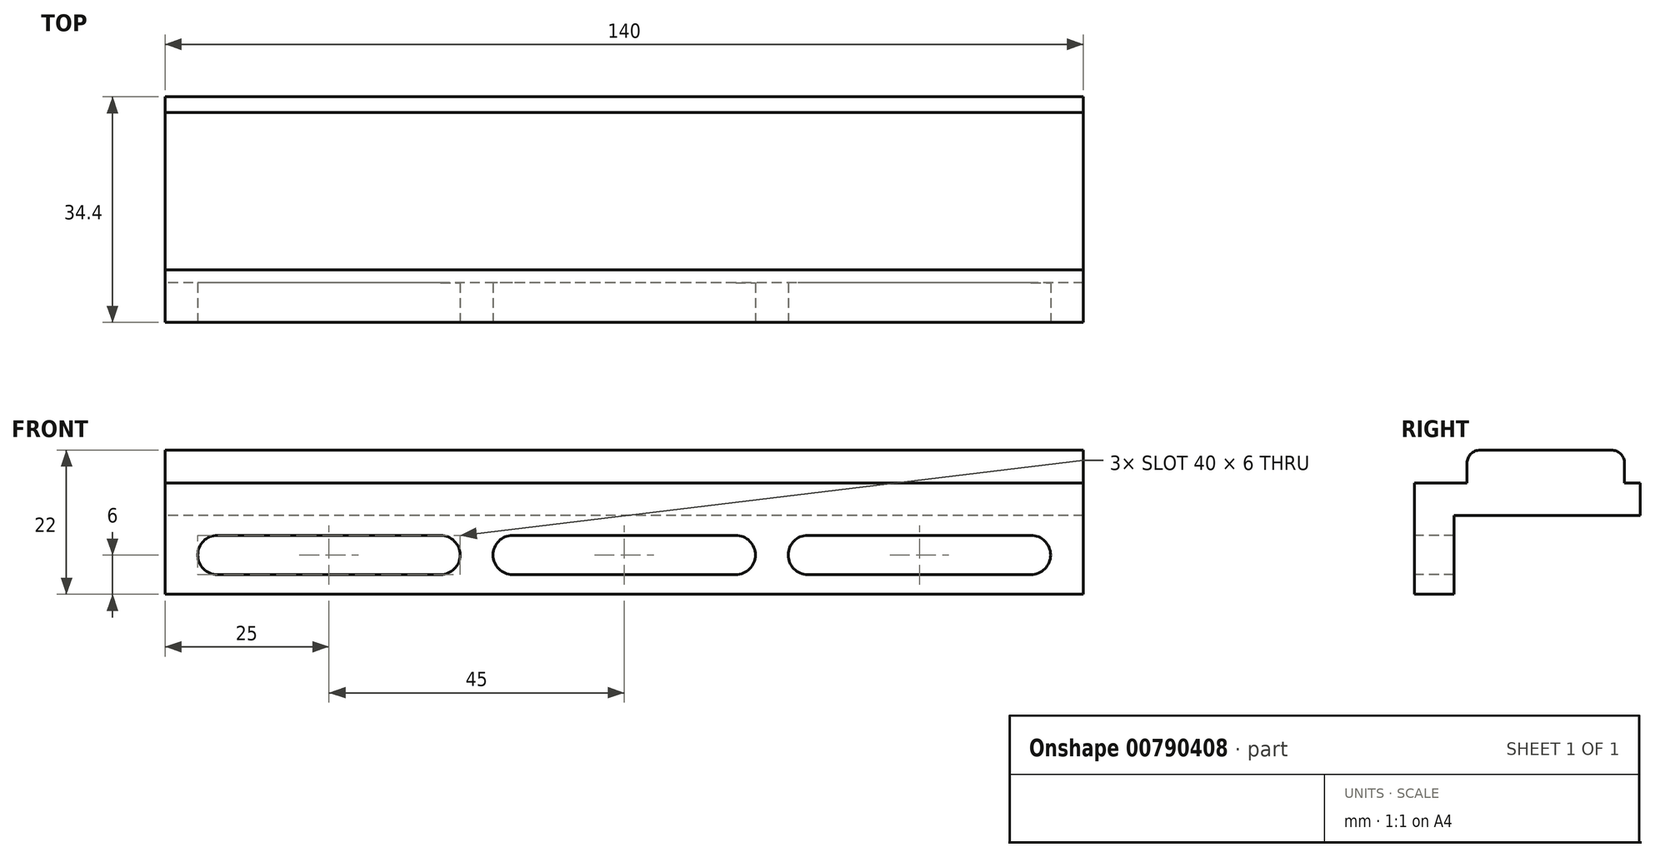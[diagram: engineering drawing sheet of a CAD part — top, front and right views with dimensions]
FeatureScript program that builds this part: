
annotation { "Feature Type Name" : "Feature", "Feature Type Description" : "" }
export const myFeature = defineFeature(function(context is Context, id is Id, definition is map)
    precondition{}
    {
        {
            var Q0;
            Q0=qCreatedBy(makeId("Right.planeOp"),FACE);
            var sketch = newSketch(context, id + "F0", { "sketchPlane" : qUnion([Q0])});
            skLineSegment(sketch, "E0", {"start": v(-20, -12) * mm, "end": v(-20, 5) * mm});
            skLineSegment(sketch, "E1", {"start": v(-20, 5) * mm, "end": v(-12, 5) * mm});
            skLineSegment(sketch, "E2", {"start": v(-12, 5) * mm, "end": v(-12, 10) * mm});
            skLineSegment(sketch, "E3", {"start": v(-12, 10) * mm, "end": v(12, 10) * mm});
            skLineSegment(sketch, "E4", {"start": v(12, 10) * mm, "end": v(12, 5) * mm});
            skLineSegment(sketch, "E5", {"start": v(12, 5) * mm, "end": v(14.4, 5) * mm});
            skLineSegment(sketch, "E6", {"start": v(14.4, 5) * mm, "end": v(14.4, 0) * mm});
            skLineSegment(sketch, "E7", {"start": v(14.4, 0) * mm, "end": v(-14, 0) * mm});
            skLineSegment(sketch, "E8", {"start": v(-14, 0) * mm, "end": v(-14, -12) * mm});
            skLineSegment(sketch, "E9", {"start": v(-14, -12) * mm, "end": v(-20, -12) * mm});
            skLineSegment(sketch, "E10", {"start": v(0, 10) * mm, "end": v(0, 0) * mm, "construction": true});
            skSolve(sketch);
        }
        {
            var Q0;
            Q0=makeQuery(id+"F0.imprint","IMPRINT",FACE,{"disambiguationData":[TD([[makeQuery(id+"F0.imprint","IMPRINT",EDGE,{"derivedFrom":sQuery(id+"F0.wireOp",EDGE,"E0")}),-1.0]])]});
            extrude(context, id + "F1", {"entities" : qUnion([Q0]), "endBound" : BoundingType.SYMMETRIC, "depth" : 140 * mm, "offsetDistance" : 25 * mm});
        }
        {
            var Q0;
            Q0=makeQuery(id+"F1.opExtrude","SWEPT_EDGE",EDGE,{"disambiguationData":[OSD([sQuery(id+"F0.wireOp",EDGE,"E2"),sQuery(id+"F0.wireOp",EDGE,"E3")])]});
            var Q1;
            Q1=makeQuery(id+"F1.opExtrude","SWEPT_EDGE",EDGE,{"disambiguationData":[OSD([sQuery(id+"F0.wireOp",EDGE,"E3"),sQuery(id+"F0.wireOp",EDGE,"E4")])]});
            fillet(context, id + "F2", {"entities" : qUnion([Q0, Q1]), "radius" : 2 * mm, "tangentPropagation" : true, "allowEdgeOverflow" : false});
        }
        {
            var Q0;
            Q0=makeQuery(id+"F1.opExtrude","SWEPT_FACE",FACE,{"disambiguationData":[OSD([sQuery(id+"F0.wireOp",EDGE,"E0")])]});
            var sketch = newSketch(context, id + "F3", { "sketchPlane" : qUnion([Q0])});
            skLineSegment(sketch, "E11", {"start": v(-70, -6) * mm, "end": v(70, -6) * mm, "construction": true});
            skLineSegment(sketch, "E12.bottom", {"start": v(-62, -3) * mm, "end": v(-28, -3) * mm});
            skLineSegment(sketch, "E12.top", {"start": v(-62, -9) * mm, "end": v(-28, -9) * mm});
            skLineSegment(sketch, "E12.left", {"start": v(-65, -6) * mm, "end": v(-65, -6) * mm});
            skLineSegment(sketch, "E12.right", {"start": v(-25, -6) * mm, "end": v(-25, -6) * mm});
            skPoint(sketch, "E13.visualSharp", {"position": v(-65, -3) * mm});
            skArc(sketch, "E13.filletArc", {"start": v(-62, -3) * mm, "mid": v(-64.12, -3.88) * mm, "end": v(-65, -6) * mm});
            skPoint(sketch, "E14.visualSharp", {"position": v(-65, -9) * mm});
            skArc(sketch, "E14.filletArc", {"start": v(-65, -6) * mm, "mid": v(-64.12, -8.12) * mm, "end": v(-62, -9) * mm});
            skPoint(sketch, "E15.visualSharp", {"position": v(-25, -9) * mm});
            skArc(sketch, "E15.filletArc", {"start": v(-28, -9) * mm, "mid": v(-25.88, -8.12) * mm, "end": v(-25, -6) * mm});
            skPoint(sketch, "E16.visualSharp", {"position": v(-25, -3) * mm});
            skArc(sketch, "E16.filletArc", {"start": v(-25, -6) * mm, "mid": v(-25.88, -3.88) * mm, "end": v(-28, -3) * mm});
            skArc(sketch, "E17.1.0.0", {"start": v(-17, -3) * mm, "mid": v(-19.12, -3.88) * mm, "end": v(-20, -6) * mm});
            skArc(sketch, "E17.1.0.1", {"start": v(-20, -6) * mm, "mid": v(-19.12, -8.12) * mm, "end": v(-17, -9) * mm});
            skLineSegment(sketch, "E17.1.0.2", {"start": v(-17, -9) * mm, "end": v(17, -9) * mm});
            skLineSegment(sketch, "E17.1.0.3", {"start": v(-17, -3) * mm, "end": v(17, -3) * mm});
            skArc(sketch, "E17.1.0.4", {"start": v(20, -6) * mm, "mid": v(19.12, -3.88) * mm, "end": v(17, -3) * mm});
            skArc(sketch, "E17.1.0.5", {"start": v(17, -9) * mm, "mid": v(19.12, -8.12) * mm, "end": v(20, -6) * mm});
            skArc(sketch, "E17.2.0.0", {"start": v(28, -3) * mm, "mid": v(25.88, -3.88) * mm, "end": v(25, -6) * mm});
            skArc(sketch, "E17.2.0.1", {"start": v(25, -6) * mm, "mid": v(25.88, -8.12) * mm, "end": v(28, -9) * mm});
            skLineSegment(sketch, "E17.2.0.2", {"start": v(28, -9) * mm, "end": v(62, -9) * mm});
            skLineSegment(sketch, "E17.2.0.3", {"start": v(28, -3) * mm, "end": v(62, -3) * mm});
            skArc(sketch, "E17.2.0.4", {"start": v(65, -6) * mm, "mid": v(64.12, -3.88) * mm, "end": v(62, -3) * mm});
            skArc(sketch, "E17.2.0.5", {"start": v(62, -9) * mm, "mid": v(64.12, -8.12) * mm, "end": v(65, -6) * mm});
            skLineSegment(sketch, "E17.direction1", {"start": v(-65, -6) * mm, "end": v(-20, -6) * mm, "construction": true});
            skSolve(sketch);
        }
        {
            var Q0;
            Q0=makeQuery(id+"F3.imprint","IMPRINT",FACE,{"disambiguationData":[TD([[makeQuery(id+"F3.imprint","IMPRINT",EDGE,{"derivedFrom":sQuery(id+"F3.wireOp",EDGE,"E12.bottom")}),-1.0]])]});
            var Q1;
            Q1=makeQuery(id+"F3.imprint","IMPRINT",FACE,{"disambiguationData":[TD([[makeQuery(id+"F3.imprint","IMPRINT",EDGE,{"derivedFrom":sQuery(id+"F3.wireOp",EDGE,"E17.1.0.0")}),1.0]])]});
            var Q2;
            Q2=makeQuery(id+"F3.imprint","IMPRINT",FACE,{"disambiguationData":[TD([[makeQuery(id+"F3.imprint","IMPRINT",EDGE,{"derivedFrom":sQuery(id+"F3.wireOp",EDGE,"E17.2.0.0")}),1.0]])]});
            extrude(context, id + "F4", {"entities" : qUnion([Q0, Q1, Q2]), "operationType" : NewBodyOperationType.REMOVE, "oppositeDirection" : true, "depth" : 25 * mm, "offsetDistance" : 25 * mm});
        }
    });
